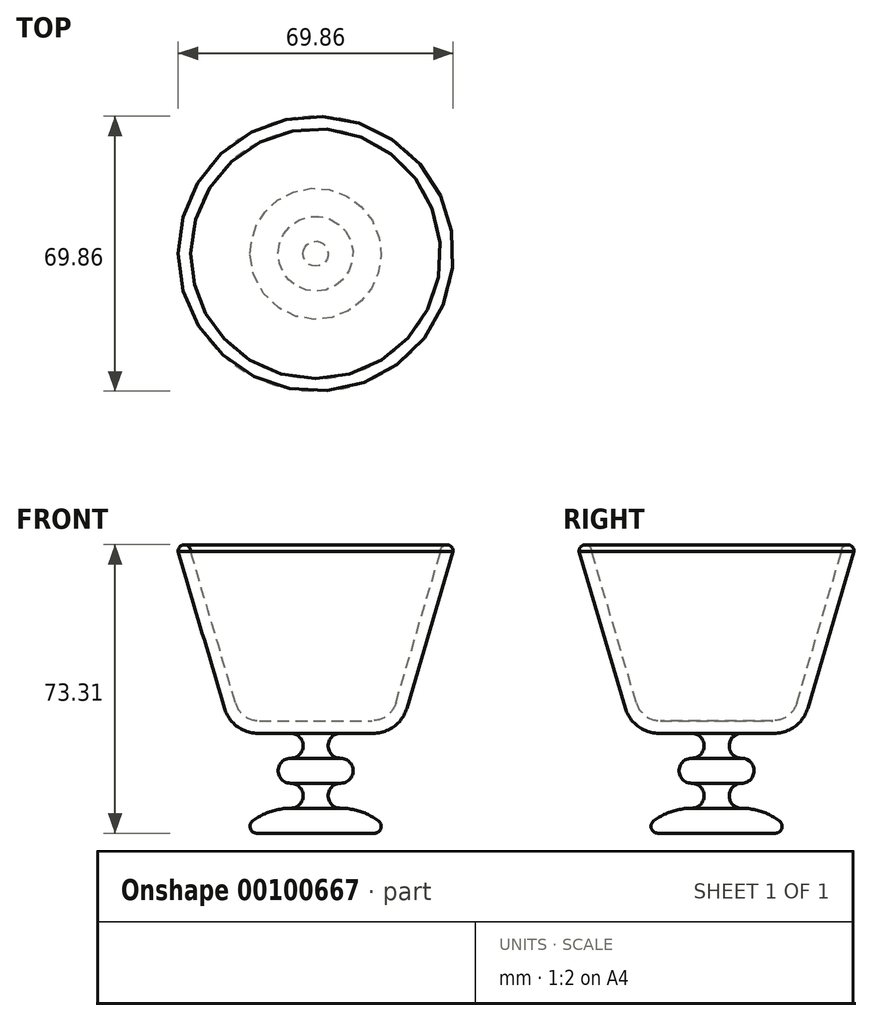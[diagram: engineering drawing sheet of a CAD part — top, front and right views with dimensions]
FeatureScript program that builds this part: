
annotation { "Feature Type Name" : "Feature", "Feature Type Description" : "" }
export const myFeature = defineFeature(function(context is Context, id is Id, definition is map)
    precondition{}
    {
        {
            var Q0;
            Q0=qCreatedBy(makeId("Front.planeOp"),FACE);
            var sketch = newSketch(context, id + "F0", { "sketchPlane" : qUnion([Q0])});
            skLineSegment(sketch, "E0", {"start": v(0, 0) * mm, "end": v(-14.3, 0) * mm});
            skLineSegment(sketch, "E1", {"start": v(-20.4, 4.55) * mm, "end": v(-31.75, 43.03) * mm});
            skLineSegment(sketch, "E2", {"start": v(-34.93, 43.03) * mm, "end": v(-23.17, 3.2) * mm});
            skLineSegment(sketch, "E3", {"start": v(-14.64, -3.18) * mm, "end": v(-6.35, -3.18) * mm});
            skArc(sketch, "E4", {"start": v(-6.35, -3.18) * mm, "mid": v(-3.17, -6.35) * mm, "end": v(-6.35, -9.53) * mm});
            skArc(sketch, "E5", {"start": v(-6.35, -9.53) * mm, "mid": v(-9.52, -12.7) * mm, "end": v(-6.35, -15.88) * mm});
            skArc(sketch, "E6", {"start": v(-6.35, -15.88) * mm, "mid": v(-3.17, -19.05) * mm, "end": v(-6.35, -22.23) * mm});
            skArc(sketch, "E7", {"start": v(-6.35, -22.23) * mm, "mid": v(-11.44, -23.06) * mm, "end": v(-15.99, -25.49) * mm});
            skLineSegment(sketch, "E8", {"start": v(-14.94, -28.58) * mm, "end": v(0, -28.58) * mm});
            skLineSegment(sketch, "E9", {"start": v(0, -28.58) * mm, "end": v(0, 0) * mm});
            skArc(sketch, "E10", {"start": v(-31.75, 43.03) * mm, "mid": v(-33.34, 44.73) * mm, "end": v(-34.93, 43.03) * mm});
            skLineSegment(sketch, "E11", {"start": v(0, 0) * mm, "end": v(0, 20.75) * mm, "construction": true});
            skPoint(sketch, "E12.visualSharp", {"position": v(-19.05, 0) * mm});
            skArc(sketch, "E12.filletArc", {"start": v(-20.4, 4.55) * mm, "mid": v(-18.1, 1.26) * mm, "end": v(-14.3, 0) * mm});
            skPoint(sketch, "E13.visualSharp", {"position": v(-21.29, -3.18) * mm});
            skArc(sketch, "E13.filletArc", {"start": v(-23.17, 3.2) * mm, "mid": v(-19.97, -1.4) * mm, "end": v(-14.64, -3.18) * mm});
            skPoint(sketch, "E14.visualSharp", {"position": v(-19.05, -28.58) * mm});
            skArc(sketch, "E14.filletArc", {"start": v(-15.99, -25.49) * mm, "mid": v(-16.57, -27.4) * mm, "end": v(-14.94, -28.58) * mm});
            skSolve(sketch);
        }
        {
            var Q0;
            Q0=makeQuery(id+"F0.imprint","IMPRINT",FACE,{"disambiguationData":[TD([[makeQuery(id+"F0.imprint","IMPRINT",EDGE,{"derivedFrom":sQuery(id+"F0.wireOp",EDGE,"E0")}),1.0]])]});
            var Q1;
            Q1=sQuery(id+"F0.wireOp",EDGE,"E11");
            revolve(context, id + "F1", {"entities" : qUnion([Q0]), "axis" : qUnion([Q1]), "revolveType" : RevolveType.FULL});
        }
    });
